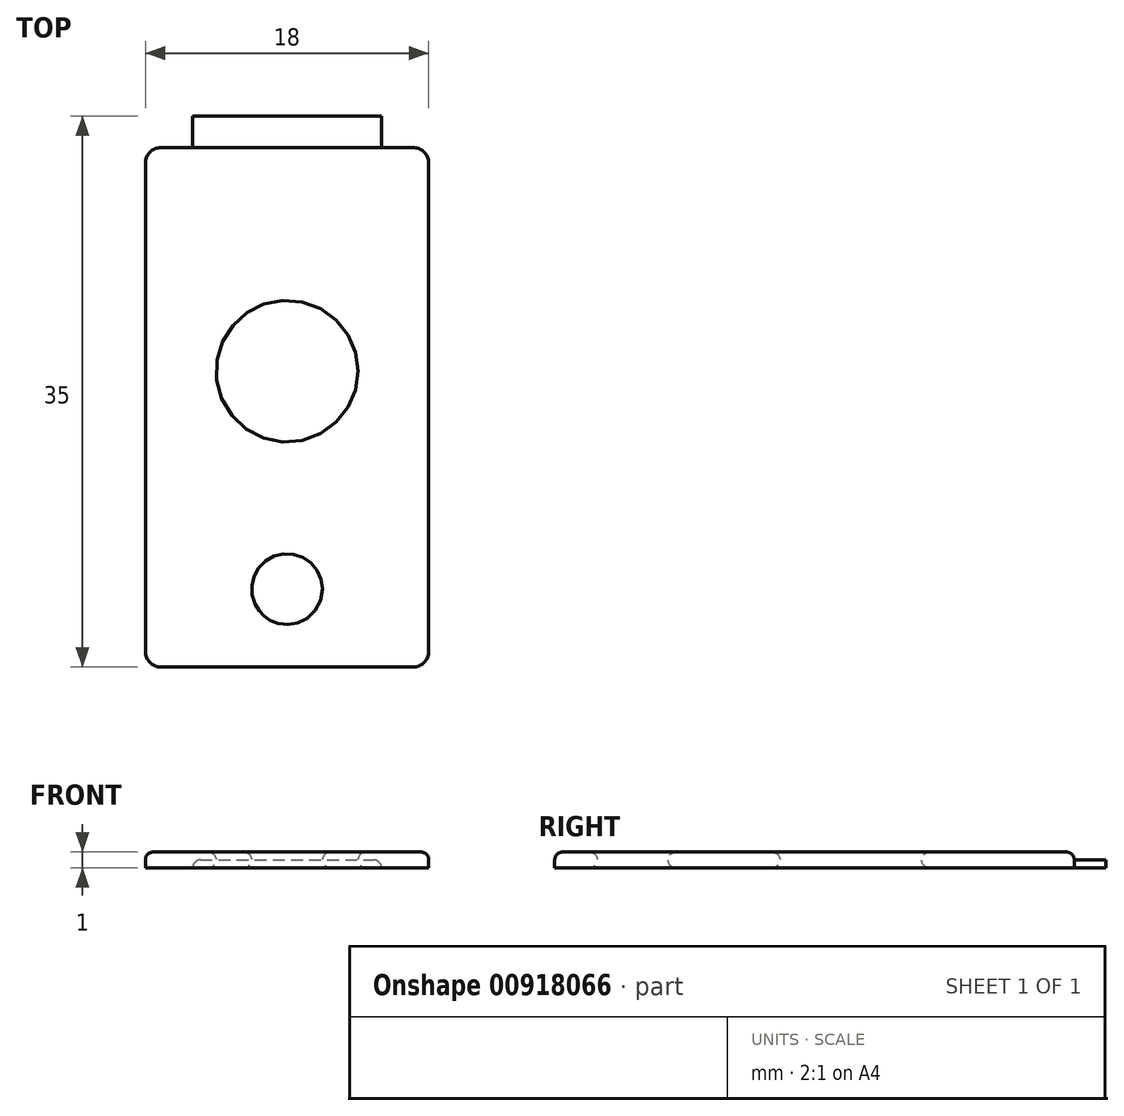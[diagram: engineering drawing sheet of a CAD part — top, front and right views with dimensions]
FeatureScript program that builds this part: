
annotation { "Feature Type Name" : "Feature", "Feature Type Description" : "" }
export const myFeature = defineFeature(function(context is Context, id is Id, definition is map)
    precondition{}
    {
        {
            var Q0;
            Q0=qCreatedBy(makeId("Top.planeOp"),FACE);
            var sketch = newSketch(context, id + "F0", { "sketchPlane" : qUnion([Q0])});
            skLineSegment(sketch, "E0", {"start": v(0, 0) * mm, "end": v(14, 0) * mm, "construction": true});
            skLineSegment(sketch, "E1", {"start": v(14, 0) * mm, "end": v(14, 29) * mm, "construction": true});
            skLineSegment(sketch, "E2", {"start": v(14, 29) * mm, "end": v(11.5, 29) * mm, "construction": true});
            skLineSegment(sketch, "E3", {"start": v(11.5, 29) * mm, "end": v(11.5, 44.5) * mm, "construction": true});
            skLineSegment(sketch, "E4", {"start": v(2.5, 44.5) * mm, "end": v(2.5, 29) * mm, "construction": true});
            skLineSegment(sketch, "E5", {"start": v(2.5, 29) * mm, "end": v(0, 29) * mm, "construction": true});
            skLineSegment(sketch, "E6", {"start": v(0, 29) * mm, "end": v(0, 0) * mm, "construction": true});
            skLineSegment(sketch, "E7", {"start": v(11.5, 44.5) * mm, "end": v(9.25, 44.5) * mm, "construction": true});
            skLineSegment(sketch, "E8", {"start": v(9.25, 44.5) * mm, "end": v(9.25, 43.5) * mm, "construction": true});
            skLineSegment(sketch, "E9", {"start": v(9.25, 43.5) * mm, "end": v(4.75, 43.5) * mm, "construction": true});
            skLineSegment(sketch, "E10", {"start": v(4.75, 43.5) * mm, "end": v(4.75, 44.5) * mm, "construction": true});
            skLineSegment(sketch, "E11", {"start": v(4.75, 44.5) * mm, "end": v(2.5, 44.5) * mm, "construction": true});
            skLineSegment(sketch, "E12", {"start": v(-1, -2) * mm, "end": v(15, -2) * mm});
            skLineSegment(sketch, "E13", {"start": v(16, -1) * mm, "end": v(16, 30) * mm});
            skLineSegment(sketch, "E14", {"start": v(15, 31) * mm, "end": v(13, 31) * mm});
            skLineSegment(sketch, "E15", {"start": v(-2, 30) * mm, "end": v(-2, -1) * mm});
            skPoint(sketch, "E16.visualSharp", {"position": v(16, 31) * mm});
            skArc(sketch, "E16.filletArc", {"start": v(16, 30) * mm, "mid": v(15.7, 30.7) * mm, "end": v(15, 31) * mm});
            skPoint(sketch, "E17.visualSharp", {"position": v(16, -2) * mm});
            skArc(sketch, "E17.filletArc", {"start": v(15, -2) * mm, "mid": v(15.7, -1.7) * mm, "end": v(16, -1) * mm});
            skPoint(sketch, "E18.visualSharp", {"position": v(-2, -2) * mm});
            skArc(sketch, "E18.filletArc", {"start": v(-2, -1) * mm, "mid": v(-1.7, -1.7) * mm, "end": v(-1, -2) * mm});
            skCircle(sketch, "E19", {"center": v(7, 16.8) * mm, "radius": 4.5 * mm});
            skCircle(sketch, "E20", {"center": v(7, 2.95) * mm, "radius": 2.25 * mm});
            skLineSegment(sketch, "E21", {"start": v(7, 43.5) * mm, "end": v(7, 0) * mm, "construction": true});
            skLineSegment(sketch, "E22", {"start": v(1, 31) * mm, "end": v(13, 31) * mm});
            skLineSegment(sketch, "E23", {"start": v(1, 31) * mm, "end": v(1, 31) * mm});
            skLineSegment(sketch, "E24", {"start": v(1, 33) * mm, "end": v(13, 33) * mm});
            skLineSegment(sketch, "E25", {"start": v(13, 33) * mm, "end": v(13, 31) * mm});
            skLineSegment(sketch, "E26", {"start": v(1, 33) * mm, "end": v(1, 31) * mm});
            skLineSegment(sketch, "E27", {"start": v(1, 31) * mm, "end": v(-1, 31) * mm});
            skPoint(sketch, "E28.visualSharp", {"position": v(-2, 31) * mm});
            skArc(sketch, "E28.filletArc", {"start": v(-1, 31) * mm, "mid": v(-1.7, 30.7) * mm, "end": v(-2, 30) * mm});
            skSolve(sketch);
        }
        {
            var Q0;
            Q0=makeQuery(id+"F0.imprint","IMPRINT",FACE,{"disambiguationData":[TD([[makeQuery(id+"F0.imprint","IMPRINT",EDGE,{"derivedFrom":sQuery(id+"F0.wireOp",EDGE,"E12")}),1.0]])]});
            extrude(context, id + "F1", {"entities" : qUnion([Q0]), "depth" : 1 * mm, "offsetDistance" : 25 * mm});
        }
        {
            var Q0;
            Q0=makeQuery(id+"F1.opExtrude","CAP_EDGE",EDGE,{"disambiguationData":[OSD([sQuery(id+"F0.wireOp",EDGE,"E19")])],"isStart":true});
            var Q1;
            Q1=makeQuery(id+"F1.opExtrude","CAP_EDGE",EDGE,{"disambiguationData":[OSD([sQuery(id+"F0.wireOp",EDGE,"E20")])],"isStart":true});
            fillet(context, id + "F2", {"entities" : qUnion([Q0, Q1]), "radius" : 0.5 * mm, "tangentPropagation" : true, "allowEdgeOverflow" : false});
        }
        {
            var Q0;
            Q0=makeQuery(id+"F0.imprint","IMPRINT",FACE,{"disambiguationData":[TD([[makeQuery(id+"F0.imprint","IMPRINT",EDGE,{"derivedFrom":sQuery(id+"F0.wireOp",EDGE,"E22")}),1.0]])]});
            extrude(context, id + "F3", {"entities" : qUnion([Q0]), "operationType" : NewBodyOperationType.ADD, "depth" : 0.5 * mm, "offsetDistance" : 25 * mm});
        }
        {
            var Q0;
            Q0=makeQuery(id+"F1.opExtrude","CAP_FACE",FACE,{"disambiguationData":[OSD([sQuery(id+"F0.wireOp",EDGE,"E12"),sQuery(id+"F0.wireOp",EDGE,"E13"),sQuery(id+"F0.wireOp",EDGE,"E14"),sQuery(id+"F0.wireOp",EDGE,"E15"),sQuery(id+"F0.wireOp",EDGE,"449a8baf-9bf3-4963-96ef-acb6162ad5c7.filletArc"),sQuery(id+"F0.wireOp",EDGE,"E16.filletArc"),sQuery(id+"F0.wireOp",EDGE,"E17.filletArc"),sQuery(id+"F0.wireOp",EDGE,"E18.filletArc"),sQuery(id+"F0.wireOp",EDGE,"E19"),sQuery(id+"F0.wireOp",EDGE,"E20"),sQuery(id+"F0.wireOp",EDGE,"C1URhJbP-0OB5-DFvt-PfT1-DFO4LItXMsE7"),sQuery(id+"F0.wireOp",EDGE,"E22")])],"isStart":false});
            fillet(context, id + "F4", {"entities" : qUnion([Q0]), "radius" : 0.5 * mm, "tangentPropagation" : true, "allowEdgeOverflow" : false});
        }
        {
            var Q0;
            Q0=makeQuery(id+"F3.opExtrude","CAP_EDGE",EDGE,{"disambiguationData":[OSD([sQuery(id+"F0.wireOp",EDGE,"E26")])],"isStart":false});
            var Q1;
            Q1=makeQuery(id+"F3.opExtrude","CAP_EDGE",EDGE,{"disambiguationData":[OSD([sQuery(id+"F0.wireOp",EDGE,"E25")])],"isStart":false});
            fillet(context, id + "F5", {"entities" : qUnion([Q0, Q1]), "radius" : 0.5 * mm, "tangentPropagation" : true, "allowEdgeOverflow" : false});
        }
    });
